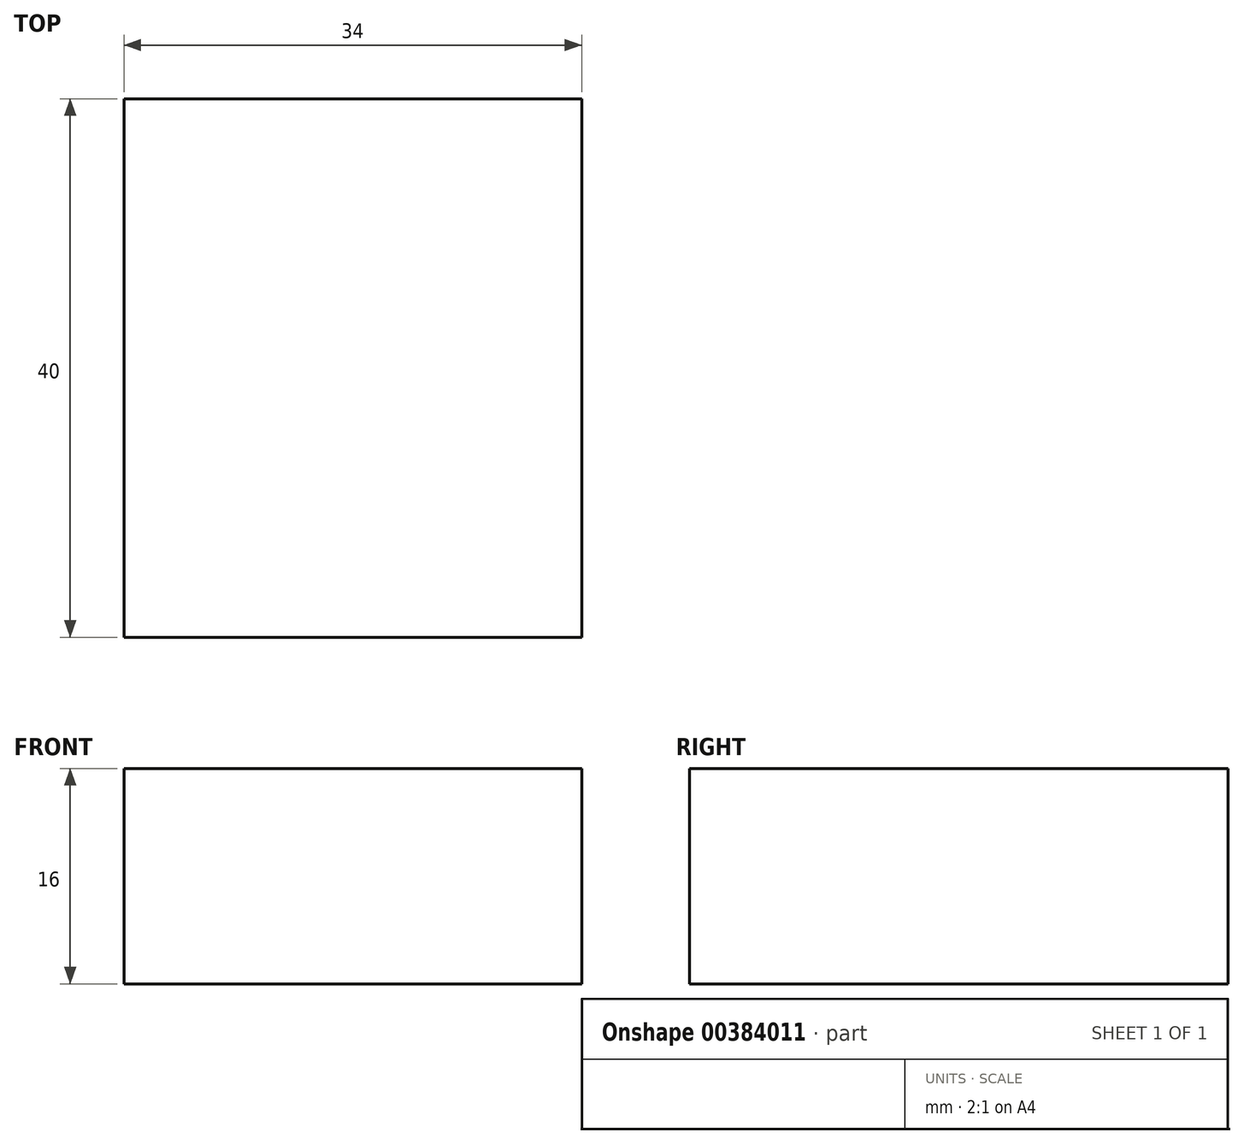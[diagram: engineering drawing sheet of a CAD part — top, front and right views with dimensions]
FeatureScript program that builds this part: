
annotation { "Feature Type Name" : "Feature", "Feature Type Description" : "" }
export const myFeature = defineFeature(function(context is Context, id is Id, definition is map)
    precondition{}
    {
        {
            var Q0;
            Q0=qCreatedBy(makeId("Front.planeOp"),FACE);
            var sketch = newSketch(context, id + "F0", { "sketchPlane" : qUnion([Q0])});
            skLineSegment(sketch, "E0.bottom", {"start": v(-17, -8) * mm, "end": v(17, -8) * mm});
            skLineSegment(sketch, "E0.top", {"start": v(-17, 8) * mm, "end": v(17, 8) * mm});
            skLineSegment(sketch, "E0.left", {"start": v(-17, -8) * mm, "end": v(-17, 8) * mm});
            skLineSegment(sketch, "E0.right", {"start": v(17, -8) * mm, "end": v(17, 8) * mm});
            skSolve(sketch);
        }
        {
            var Q0;
            Q0 = qSketchRegion(id + "F0", true);
            extrude(context, id + "F1", {"entities" : qUnion([Q0]), "depth" : 20 * mm, "hasSecondDirection" : true, "secondDirectionOppositeDirection" : true, "secondDirectionDepth" : 20 * mm});
        }
    });
